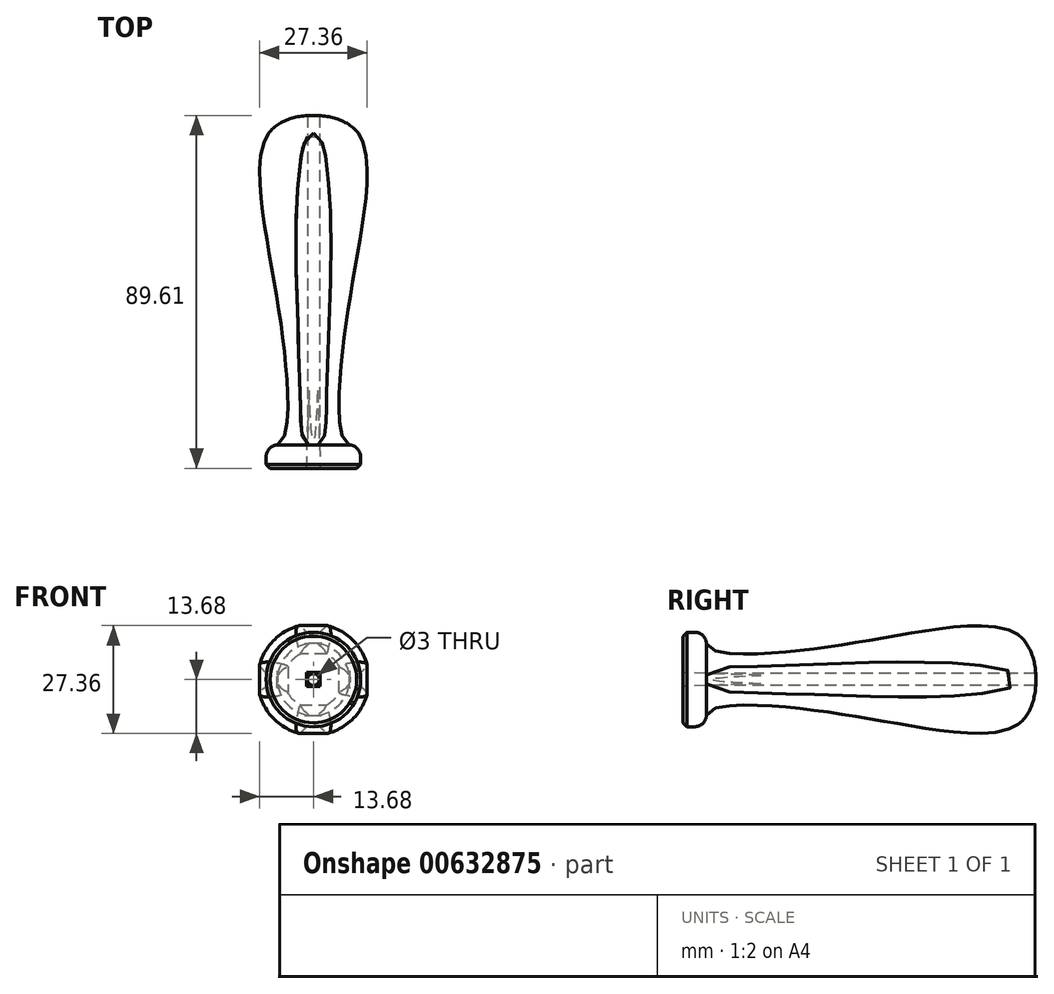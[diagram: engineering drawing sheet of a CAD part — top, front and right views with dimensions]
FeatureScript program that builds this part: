
annotation { "Feature Type Name" : "Feature", "Feature Type Description" : "" }
export const myFeature = defineFeature(function(context is Context, id is Id, definition is map)
    precondition{}
    {
        {
            var Q0;
            Q0=qCreatedBy(makeId("Right.planeOp"),FACE);
            var sketch = newSketch(context, id + "F0", { "sketchPlane" : qUnion([Q0])});
            skLineSegment(sketch, "E0", {"start": v(0, 0) * mm, "end": v(0, 12) * mm});
            skLineSegment(sketch, "E1", {"start": v(0, 12) * mm, "end": v(2.93, 12) * mm});
            skLineSegment(sketch, "E2", {"start": v(81.16, 0) * mm, "end": v(0, 0) * mm});
            skPoint(sketch, "E3.visualSharp", {"position": v(4, 12) * mm});
            skArc(sketch, "E3.filletArc", {"start": v(5.92, 9.15) * mm, "mid": v(5, 11.17) * mm, "end": v(2.93, 12) * mm});
            skFitSpline(sketch, "E4", {"points": [v(5.92, 9.15) * mm, v(36.67, 9.15) * mm, v(83.7, 12.32) * mm, v(89.66, 0) * mm], "startDerivative": vector(8.43, -24.25) * mm, "endDerivative": vector(0, -60.02) * mm});
            skLineSegment(sketch, "E5", {"start": v(81.16, 0) * mm, "end": v(100.7, 0) * mm});
            skFitSpline(sketch, "E6.0", {"points": [v(4.79, 8.76) * mm, v(4.84, 8.61) * mm, v(4.97, 8.34) * mm, v(5.32, 7.87) * mm, v(5.84, 7.45) * mm, v(6.56, 7.08) * mm, v(7.36, 6.8) * mm, v(8.28, 6.58) * mm, v(9.63, 6.34) * mm, v(11.6, 6.15) * mm, v(14.38, 6.07) * mm, v(17.51, 6.11) * mm, v(20.96, 6.27) * mm, v(25.9, 6.64) * mm, v(31.25, 7.2) * mm, v(36.78, 7.94) * mm, v(40.95, 8.57) * mm, v(45.1, 9.25) * mm, v(50.6, 10.18) * mm, v(57.33, 11.32) * mm, v(64.91, 12.42) * mm, v(71.77, 13.04) * mm, v(76.66, 12.96) * mm, v(79.94, 12.45) * mm, v(81.7, 11.94) * mm, v(82.9, 11.4) * mm, v(83.98, 10.8) * mm, v(85.13, 9.88) * mm, v(86.24, 8.56) * mm, v(87.39, 6.55) * mm, v(88.27, 3.64) * mm, v(88.46, 1.19) * mm, v(88.46, 0) * mm]});
            skSolve(sketch);
        }
        {
            var Q0;
            Q0=makeQuery(id+"F0.imprint","IMPRINT",FACE,{"disambiguationData":[TD([[makeQuery(id+"F0.imprint","IMPRINT",EDGE,{"derivedFrom":sQuery(id+"F0.wireOp",EDGE,"E0")}),-1.0]])]});
            var Q1;
            Q1=sQuery(id+"F0.wireOp",EDGE,"E2");
            revolve(context, id + "F1", {"entities" : qUnion([Q0]), "axis" : qUnion([Q1]), "revolveType" : RevolveType.FULL});
        }
        {
            var Q0;
            Q0=makeQuery(id+"F1.opRevolve","SWEPT_EDGE",EDGE,{"disambiguationData":[OSD([sQuery(id+"F0.wireOp",EDGE,"E0"),sQuery(id+"F0.wireOp",EDGE,"E1")])]});
            chamfer(context, id + "F2", {"entities" : qUnion([Q0]), "width" : 1 * mm, "tangentPropagation" : true});
        }
        {
            var Q0;
            Q0=qCreatedBy(makeId("Right.planeOp"),FACE);
            var sketch = newSketch(context, id + "F3", { "sketchPlane" : qUnion([Q0])});
            skLineSegment(sketch, "E7", {"start": v(0, 0) * mm, "end": v(0, 12) * mm});
            skLineSegment(sketch, "E8", {"start": v(81.16, 0) * mm, "end": v(0, 0) * mm});
            skPoint(sketch, "E9.visualSharp", {"position": v(4, 12) * mm});
            skLineSegment(sketch, "E10", {"start": v(81.16, 0) * mm, "end": v(100.7, 0) * mm});
            skFitSpline(sketch, "E11.0", {"points": [v(5.9, 9.16) * mm, v(5.95, 9.01) * mm, v(6.08, 8.74) * mm, v(6.43, 8.28) * mm, v(6.95, 7.85) * mm, v(7.67, 7.48) * mm, v(8.48, 7.2) * mm, v(9.39, 6.99) * mm, v(10.75, 6.76) * mm, v(12.72, 6.57) * mm, v(15.5, 6.5) * mm, v(18.63, 6.55) * mm, v(22.08, 6.72) * mm, v(27.02, 7.1) * mm, v(32.37, 7.68) * mm, v(37.89, 8.44) * mm, v(42.05, 9.08) * mm, v(46.21, 9.77) * mm, v(51.71, 10.71) * mm, v(58.43, 11.87) * mm, v(66, 13) * mm, v(72.86, 13.63) * mm, v(77.76, 13.57) * mm, v(81.03, 13.07) * mm, v(82.79, 12.56) * mm, v(84, 12.04) * mm, v(85.08, 11.43) * mm, v(86.23, 10.52) * mm, v(87.34, 9.2) * mm, v(88.5, 7.2) * mm, v(89.39, 4.3) * mm, v(89.59, 1.83) * mm, v(89.59, 0.65) * mm]});
            skLineSegment(sketch, "E12", {"start": v(5.9, 9.16) * mm, "end": v(9.9, 31.07) * mm});
            skLineSegment(sketch, "E13", {"start": v(9.9, 31.07) * mm, "end": v(93.13, 31.07) * mm});
            skLineSegment(sketch, "E14", {"start": v(93.13, 31.07) * mm, "end": v(87.07, 9.49) * mm});
            skSolve(sketch);
        }
        {
            var Q0;
            Q0=makeQuery(id+"F3.imprint","IMPRINT",FACE,{"disambiguationData":[TD([[makeQuery(id+"F3.imprint","IMPRINT",EDGE,{"derivedFrom":sQuery(id+"F3.wireOp",EDGE,"E11.0")}),1.0]])]});
            extrude(context, id + "F4", {"entities" : qUnion([Q0]), "depth" : 5 * mm, "offsetDistance" : 25 * mm, "hasSecondDirection" : true, "secondDirectionOppositeDirection" : true, "secondDirectionDepth" : 5 * mm});
        }
        {
            var Q0;
            Q0=makeQuery(id+"F4.opExtrude","SWEPT_BODY",BODY,{"disambiguationData":[OSD([sQuery(id+"F3.wireOp",EDGE,"E11.0"),sQuery(id+"F3.wireOp",EDGE,"E12"),sQuery(id+"F3.wireOp",EDGE,"E13"),sQuery(id+"F3.wireOp",EDGE,"E14")])]});
            var Q1;
            {var subQ0=sQuery(id+"F0.wireOp",EDGE,"E0");Q1=makeQuery(id+"F2.opChamfer","BLEND_EDGE",EDGE,{"blendedFrom":[makeQuery(id+"F1.opRevolve","SWEPT_EDGE",EDGE,{"disambiguationData":[OSD([subQ0,sQuery(id+"F0.wireOp",EDGE,"E1")])]}),makeQuery(id+"F1.opRevolve","SWEPT_FACE",FACE,{"disambiguationData":[OSD([subQ0])]})],"blendedInto":[makeQuery(id+"F1.opRevolve","SWEPT_FACE",FACE,{"disambiguationData":[OSD([subQ0])]})]});}
            circularPattern(context, id + "F5", {"entities" : qUnion([Q0]), "axis" : qUnion([Q1]), "angle" : 360 * degree, "instanceCount" : 4, "equalSpace" : true});
        }
        {
            var Q0;
            Q0=makeQuery(id+"F4.opExtrude","SWEPT_BODY",BODY,{"disambiguationData":[OSD([sQuery(id+"F3.wireOp",EDGE,"E11.0"),sQuery(id+"F3.wireOp",EDGE,"E12"),sQuery(id+"F3.wireOp",EDGE,"E13"),sQuery(id+"F3.wireOp",EDGE,"E14")])]});
            var Q1;
            Q1=makeQuery(id+"F5.opPattern","COPY",BODY,{"derivedFrom":makeQuery(id+"F4.opExtrude","SWEPT_BODY",BODY,{"disambiguationData":[OSD([sQuery(id+"F3.wireOp",EDGE,"E11.0"),sQuery(id+"F3.wireOp",EDGE,"E12"),sQuery(id+"F3.wireOp",EDGE,"E13"),sQuery(id+"F3.wireOp",EDGE,"E14")])]}),"instanceName":"1"});
            var Q2;
            Q2=makeQuery(id+"F5.opPattern","COPY",BODY,{"derivedFrom":makeQuery(id+"F4.opExtrude","SWEPT_BODY",BODY,{"disambiguationData":[OSD([sQuery(id+"F3.wireOp",EDGE,"E11.0"),sQuery(id+"F3.wireOp",EDGE,"E12"),sQuery(id+"F3.wireOp",EDGE,"E13"),sQuery(id+"F3.wireOp",EDGE,"E14")])]}),"instanceName":"2"});
            var Q3;
            Q3=makeQuery(id+"F5.opPattern","COPY",BODY,{"derivedFrom":makeQuery(id+"F4.opExtrude","SWEPT_BODY",BODY,{"disambiguationData":[OSD([sQuery(id+"F3.wireOp",EDGE,"E11.0"),sQuery(id+"F3.wireOp",EDGE,"E12"),sQuery(id+"F3.wireOp",EDGE,"E13"),sQuery(id+"F3.wireOp",EDGE,"E14")])]}),"instanceName":"3"});
            var Q4;
            Q4=makeQuery(id+"F1.opRevolve","SWEPT_BODY",BODY,{"disambiguationData":[OSD([sQuery(id+"F0.wireOp",EDGE,"E0"),sQuery(id+"F0.wireOp",EDGE,"E1"),sQuery(id+"F0.wireOp",EDGE,"E2"),sQuery(id+"F0.wireOp",EDGE,"E3.filletArc"),sQuery(id+"F0.wireOp",EDGE,"E4"),sQuery(id+"F0.wireOp",EDGE,"E5")])]});
            booleanBodies(context, id + "F6", {"operationType" : BooleanOperationType.SUBTRACTION, "tools" : qUnion([Q0, Q1, Q2, Q3]), "targets" : qUnion([Q4])});
        }
        {
            var Q0;
            Q0=qCreatedBy(makeId("Front.planeOp"),FACE);
            var sketch = newSketch(context, id + "F7", { "sketchPlane" : qUnion([Q0])});
            skCircle(sketch, "E15", {"center": v(0, 0) * mm, "radius": 1.5 * mm});
            skSolve(sketch);
        }
        {
            var Q0;
            Q0=qSketchRegion(id+"F7",true);
            extrude(context, id + "F8", {"entities" : qUnion([Q0]), "operationType" : NewBodyOperationType.REMOVE, "oppositeDirection" : true, "depth" : 100 * mm, "offsetDistance" : 25 * mm, "hasSecondDirection" : true, "secondDirectionOppositeDirection" : false, "secondDirectionDepth" : 25 * mm});
        }
        {
            var Q0;
            Q0=qCreatedBy(makeId("Front.planeOp"),FACE);
            var sketch = newSketch(context, id + "F9", { "sketchPlane" : qUnion([Q0])});
            skLineSegment(sketch, "E16.bottom", {"start": v(-1.75, 1.75) * mm, "end": v(1.75, 1.75) * mm});
            skLineSegment(sketch, "E16.top", {"start": v(-1.75, -1.75) * mm, "end": v(1.75, -1.75) * mm});
            skLineSegment(sketch, "E16.left", {"start": v(-1.75, 1.75) * mm, "end": v(-1.75, -1.75) * mm});
            skLineSegment(sketch, "E16.right", {"start": v(1.75, 1.75) * mm, "end": v(1.75, -1.75) * mm});
            skPoint(sketch, "E16.middle", {"position": v(0, 0) * mm});
            skSolve(sketch);
        }
        {
            var Q0;
            Q0=qSketchRegion(id+"F9",true);
            extrude(context, id + "F10", {"entities" : qUnion([Q0]), "operationType" : NewBodyOperationType.REMOVE, "oppositeDirection" : true, "depth" : 25 * mm, "offsetDistance" : 25 * mm, "hasDraft" : true, "draftAngle" : 2 * degree, "draftPullDirection" : true});
        }
    });
